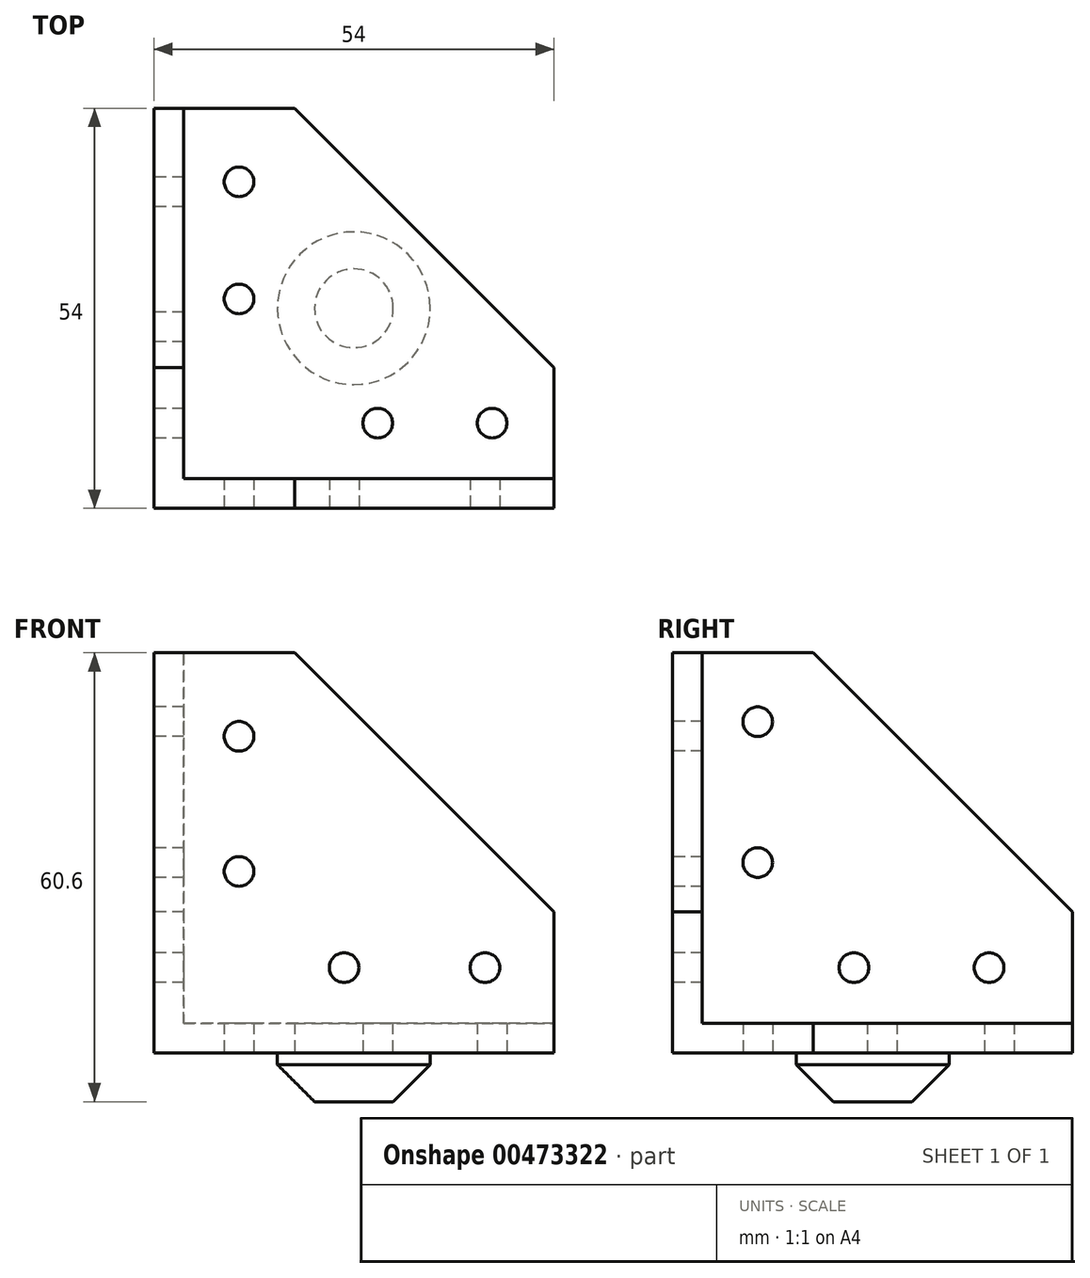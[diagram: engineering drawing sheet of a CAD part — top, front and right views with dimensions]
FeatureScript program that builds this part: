
annotation { "Feature Type Name" : "Feature", "Feature Type Description" : "" }
export const myFeature = defineFeature(function(context is Context, id is Id, definition is map)
    precondition{}
    {
        {
            var Q0;
            Q0=qCreatedBy(makeId("Top.planeOp"),FACE);
            var sketch = newSketch(context, id + "F0", { "sketchPlane" : qUnion([Q0])});
            skLineSegment(sketch, "E0.top", {"start": v(0, 50) * mm, "end": v(15, 50) * mm});
            skLineSegment(sketch, "E0.right", {"start": v(50, 0) * mm, "end": v(50, 15) * mm});
            skLineSegment(sketch, "E1.top", {"start": v(0, 15) * mm, "end": v(15, 15) * mm, "construction": true});
            skLineSegment(sketch, "E1.right", {"start": v(15, 0) * mm, "end": v(15, 15) * mm, "construction": true});
            skLineSegment(sketch, "E2", {"start": v(15, 15) * mm, "end": v(15, 50) * mm, "construction": true});
            skLineSegment(sketch, "E3", {"start": v(15, 15) * mm, "end": v(50, 15) * mm, "construction": true});
            skLineSegment(sketch, "E4", {"start": v(15, 50) * mm, "end": v(50, 15) * mm});
            skLineSegment(sketch, "E5.bottom", {"start": v(0, 50) * mm, "end": v(-4, 50) * mm});
            skLineSegment(sketch, "E5.right", {"start": v(-4, 50) * mm, "end": v(-4, 0) * mm});
            skLineSegment(sketch, "E6", {"start": v(50, 0) * mm, "end": v(50, -4) * mm});
            skLineSegment(sketch, "E7", {"start": v(50, -4) * mm, "end": v(-4, -4) * mm});
            skLineSegment(sketch, "E8", {"start": v(-4, -4) * mm, "end": v(-4, 0) * mm});
            skPoint(sketch, "E9", {"position": v(7.5, 50) * mm});
            skPoint(sketch, "E10", {"position": v(50, 7.5) * mm});
            skCircle(sketch, "E11", {"center": v(7.5, 40.07) * mm, "radius": 2 * mm});
            skCircle(sketch, "E12", {"center": v(7.5, 24.27) * mm, "radius": 2 * mm});
            skCircle(sketch, "E13", {"center": v(26.22, 7.5) * mm, "radius": 2 * mm});
            skPoint(sketch, "E13.centerSnap0", {"position": v(15, 7.5) * mm});
            skCircle(sketch, "E14", {"center": v(41.65, 7.5) * mm, "radius": 2 * mm});
            skSolve(sketch);
        }
        {
            var Q0;
            Q0=qSketchRegion(id+"F0",true);
            extrude(context, id + "F1", {"entities" : qUnion([Q0]), "depth" : 4 * mm});
        }
        {
            var Q0;
            Q0=makeQuery(id+"F1.opExtrude","SWEPT_FACE",FACE,{"disambiguationData":[OSD([sQuery(id+"F0.wireOp",EDGE,"E7")])]});
            var sketch = newSketch(context, id + "F2", { "sketchPlane" : qUnion([Q0])});
            skLineSegment(sketch, "E15", {"start": v(-4, 4) * mm, "end": v(-4, 54) * mm});
            skLineSegment(sketch, "E16", {"start": v(-4, 54) * mm, "end": v(15, 54) * mm});
            skLineSegment(sketch, "E17", {"start": v(50, 4) * mm, "end": v(50, 19) * mm});
            skLineSegment(sketch, "E18", {"start": v(50, 19) * mm, "end": v(15, 54) * mm});
            skPoint(sketch, "E19", {"position": v(7.5, 54) * mm});
            skPoint(sketch, "E20", {"position": v(50, 11.5) * mm});
            skCircle(sketch, "E21", {"center": v(7.5, 42.72) * mm, "radius": 2 * mm});
            skCircle(sketch, "E22", {"center": v(7.5, 24.48) * mm, "radius": 2 * mm});
            skCircle(sketch, "E23", {"center": v(40.7, 11.5) * mm, "radius": 2 * mm});
            skCircle(sketch, "E24", {"center": v(21.68, 11.5) * mm, "radius": 2 * mm});
            skLineSegment(sketch, "E25", {"start": v(-4, 4) * mm, "end": v(50, 4) * mm});
            skSolve(sketch);
        }
        {
            var Q0;
            Q0=qSketchRegion(id+"F2",true);
            extrude(context, id + "F3", {"entities" : qUnion([Q0]), "operationType" : NewBodyOperationType.ADD, "oppositeDirection" : true, "depth" : 4 * mm});
        }
        {
            var Q0;
            Q0=makeQuery(id+"F3.boolean.opBoolean","MERGE",FACE,{"derivedFrom":[makeQuery(id+"F1.opExtrude","SWEPT_FACE",FACE,{"disambiguationData":[OSD([sQuery(id+"F0.wireOp",EDGE,"E5.right"),sQuery(id+"F0.wireOp",EDGE,"E8")])]}),makeQuery(id+"F3.opExtrude","SWEPT_FACE",FACE,{"disambiguationData":[OSD([sQuery(id+"F2.wireOp",EDGE,"E15")])]})]});
            var sketch = newSketch(context, id + "F4", { "sketchPlane" : qUnion([Q0])});
            skLineSegment(sketch, "E26", {"start": v(0, 0) * mm, "end": v(-50, 0) * mm});
            skLineSegment(sketch, "E27", {"start": v(-50, 0) * mm, "end": v(-50, 19) * mm});
            skLineSegment(sketch, "E28", {"start": v(0, 54) * mm, "end": v(-15, 54) * mm});
            skLineSegment(sketch, "E29", {"start": v(-15, 54) * mm, "end": v(-50, 19) * mm});
            skPoint(sketch, "E30", {"position": v(-50, 11.5) * mm});
            skPoint(sketch, "E31", {"position": v(-7.5, 54) * mm});
            skCircle(sketch, "E32", {"center": v(-38.72, 11.5) * mm, "radius": 2 * mm});
            skCircle(sketch, "E33", {"center": v(-20.48, 11.5) * mm, "radius": 2 * mm});
            skCircle(sketch, "E34", {"center": v(-7.5, 44.7) * mm, "radius": 2 * mm});
            skCircle(sketch, "E35", {"center": v(-7.5, 25.68) * mm, "radius": 2 * mm});
            skLineSegment(sketch, "E36", {"start": v(0, 0) * mm, "end": v(0, 54) * mm});
            skSolve(sketch);
        }
        {
            var Q0;
            Q0=qSketchRegion(id+"F4",true);
            extrude(context, id + "F5", {"entities" : qUnion([Q0]), "operationType" : NewBodyOperationType.ADD, "oppositeDirection" : true, "depth" : 4 * mm});
        }
        {
            var Q0;
            Q0=makeQuery(id+"F1.opExtrude","CAP_FACE",FACE,{"disambiguationData":[OSD([sQuery(id+"F0.wireOp",EDGE,"E0.top"),sQuery(id+"F0.wireOp",EDGE,"E0.right"),sQuery(id+"F0.wireOp",EDGE,"E4"),sQuery(id+"F0.wireOp",EDGE,"E5.bottom"),sQuery(id+"F0.wireOp",EDGE,"E5.right"),sQuery(id+"F0.wireOp",EDGE,"E6"),sQuery(id+"F0.wireOp",EDGE,"E7"),sQuery(id+"F0.wireOp",EDGE,"E8"),sQuery(id+"F0.wireOp",EDGE,"E11"),sQuery(id+"F0.wireOp",EDGE,"E12"),sQuery(id+"F0.wireOp",EDGE,"E13"),sQuery(id+"F0.wireOp",EDGE,"E14")])],"isStart":true});
            var sketch = newSketch(context, id + "F6", { "sketchPlane" : qUnion([Q0])});
            skCircle(sketch, "E37", {"center": v(23, -23) * mm, "radius": 10.31 * mm});
            skPoint(sketch, "E37.centerSnap0", {"position": v(23, 4) * mm});
            skPoint(sketch, "E37.centerSnap1", {"position": v(-4, -23) * mm});
            skSolve(sketch);
        }
        {
            var Q0;
            Q0 = qSketchRegion(id + "F6", true);
            extrude(context, id + "F7", {"entities" : qUnion([Q0]), "operationType" : NewBodyOperationType.ADD, "depth" : 6.6 * mm, "offsetDistance" : 25 * mm});
        }
        {
            var Q0;
            Q0=makeQuery(id+"F7.opExtrude","CAP_EDGE",EDGE,{"disambiguationData":[OSD([sQuery(id+"F6.wireOp",EDGE,"E37")])],"isStart":false});
            chamfer(context, id + "F8", {"entities" : qUnion([Q0]), "width" : 5 * mm, "tangentPropagation" : true});
        }
    });
